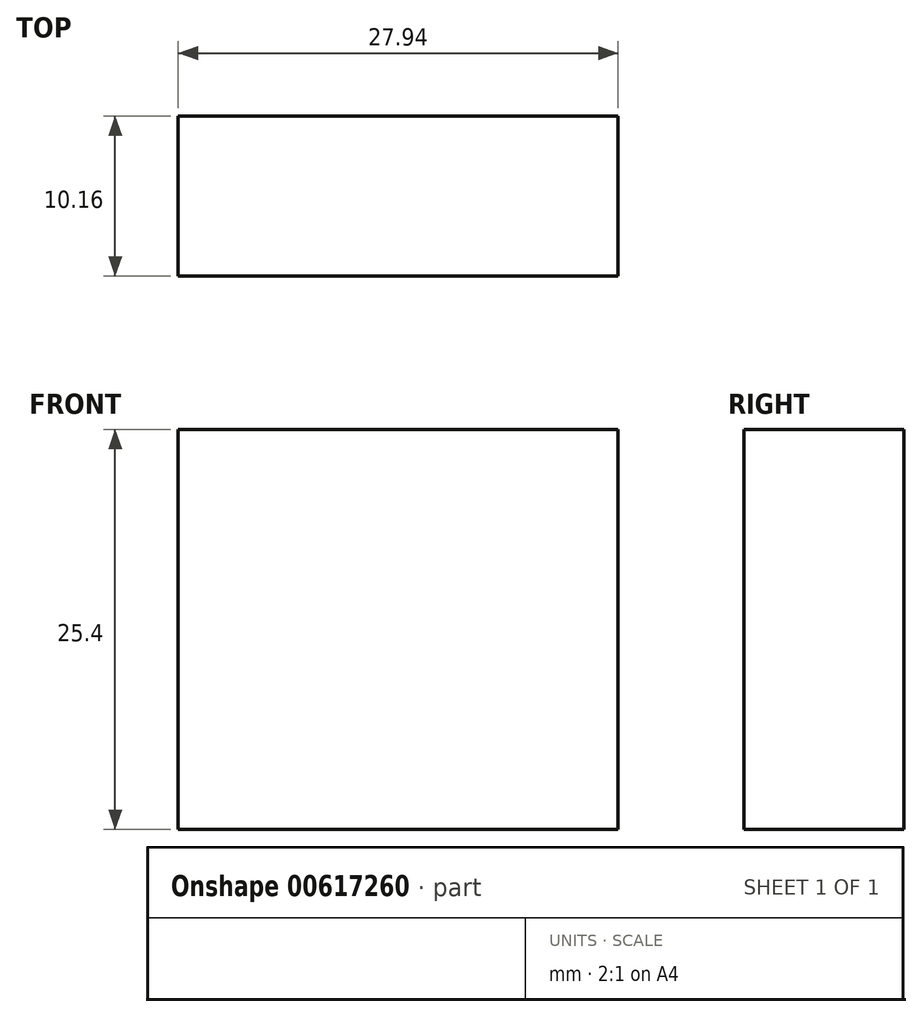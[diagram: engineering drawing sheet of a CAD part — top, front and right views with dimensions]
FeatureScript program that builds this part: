
annotation { "Feature Type Name" : "Feature", "Feature Type Description" : "" }
export const myFeature = defineFeature(function(context is Context, id is Id, definition is map)
    precondition{}
    {
        {
            var Q0;
            Q0=qCreatedBy(makeId("Top.planeOp"),FACE);
            var sketch = newSketch(context, id + "F0", { "sketchPlane" : qUnion([Q0])});
            skLineSegment(sketch, "E0.bottom", {"start": v(-18.53, 37) * mm, "end": v(9.4, 37) * mm});
            skLineSegment(sketch, "E0.top", {"start": v(-18.53, 26.85) * mm, "end": v(9.4, 26.85) * mm});
            skLineSegment(sketch, "E0.left", {"start": v(-18.53, 37) * mm, "end": v(-18.53, 26.85) * mm});
            skLineSegment(sketch, "E0.right", {"start": v(9.4, 37) * mm, "end": v(9.4, 26.85) * mm});
            skSolve(sketch);
        }
        {
            var Q0;
            Q0=makeQuery(id+"F0.imprint","IMPRINT",FACE,{"disambiguationData":[TD([[makeQuery(id+"F0.imprint","IMPRINT",EDGE,{"derivedFrom":sQuery(id+"F0.wireOp",EDGE,"E0.bottom")}),-1.0]])]});
            extrude(context, id + "F1", {"entities" : qUnion([Q0]), "depth" : 25.4 * mm, "offsetDistance" : 25.4 * mm});
        }
    });
